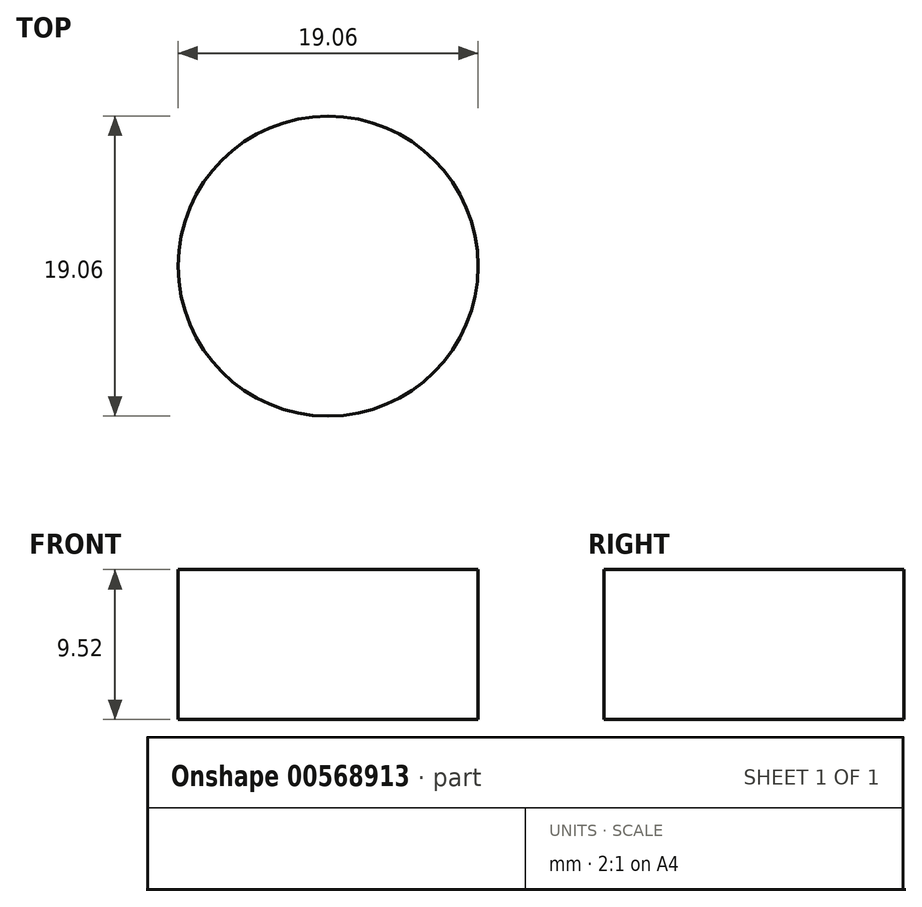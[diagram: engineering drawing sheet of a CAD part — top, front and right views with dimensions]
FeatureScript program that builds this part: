
annotation { "Feature Type Name" : "Feature", "Feature Type Description" : "" }
export const myFeature = defineFeature(function(context is Context, id is Id, definition is map)
    precondition{}
    {
        {
            var Q0;
            Q0=qCreatedBy(makeId("Top.planeOp"),FACE);
            var sketch = newSketch(context, id + "F0", { "sketchPlane" : qUnion([Q0])});
            skCircle(sketch, "E0", {"center": v(0, 0) * mm, "radius": 9.53 * mm});
            skSolve(sketch);
        }
        {
            var Q0;
            Q0=makeQuery(id+"F0.imprint","IMPRINT",FACE,{"disambiguationData":[TD([[makeQuery(id+"F0.imprint","IMPRINT",EDGE,{"derivedFrom":sQuery(id+"F0.wireOp",EDGE,"E0")}),1.0]])]});
            extrude(context, id + "F1", {"entities" : qUnion([Q0]), "endBound" : BoundingType.SYMMETRIC, "depth" : 9.52 * mm, "offsetDistance" : 25.4 * mm});
        }
    });
